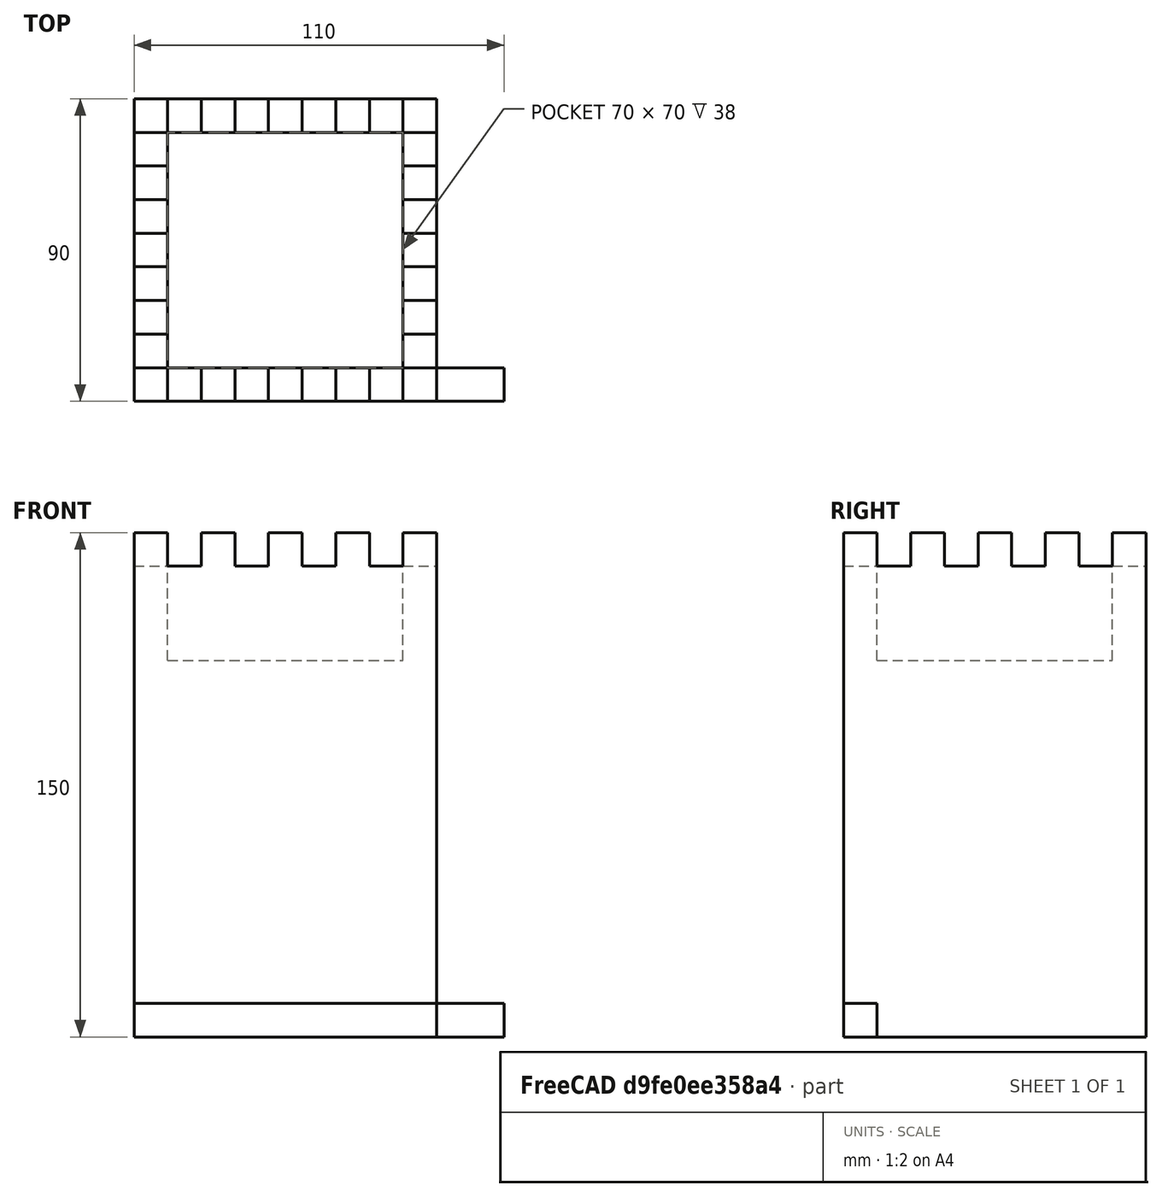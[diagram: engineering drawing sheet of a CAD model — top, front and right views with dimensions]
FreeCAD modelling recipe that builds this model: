
FCSTD DOCUMENT  (FreeCAD 1.0R39285 (Git))
Label: ojt1_t10r02_tower
License: All rights reserved
objects: Part::Box×4, Part::FeaturePython×2, Part::Cut×2, Part::MultiFuse×1
note: 7 computed .brp shape members not serialized (recipe doc carries the construction recipe); baked Part::Feature solids carry a one-line shape summary decoded from their .brp

FEATURE [Part::Box] Box  label="Cub"
  AttacherType = Attacher::AttachEngine3D
  Height = 10
  Length = 110
  Width = 10
FEATURE [Part::FeaturePython] Array  # Draft array (typed FeaturePython)
  AlwaysSyncPlacement = false
  Angle = 360
  ArrayType = 0
  Axis = (0,0,1)
  Base = -> Box
  Center = (0,0,0)
  Count = 4
  ExpandArray = false
  Fuse = false
  IntervalAxis = (0,0,0)
  IntervalX = (0,0,0)
  IntervalY = (0,20,0)
  IntervalZ = (0,0,0)
  NumberCircles = 3
  NumberPolar = 5
  NumberX = 1
  NumberY = 4
  NumberZ = 1
  PlacementList = 4 placements: arithmetic series from (0,0,0) step (0,20,0) to (0,60,0)
  RadialDistance = 50
  ScaleList = (4) [(1,1,1),(1,1,1),(1,1,1),(1,1,1)]
  Symmetry = 1
  TangentialDistance = 25
FEATURE [Part::Box] Box001  label="Cub001"
  AttacherType = Attacher::AttachEngine3D
  Height = 10
  Length = 110
  Width = 10
FEATURE [Part::FeaturePython] Array001  # Draft array (typed FeaturePython)
  AlwaysSyncPlacement = false
  Angle = 360
  ArrayType = 0
  Axis = (0,0,1)
  Base = -> Box001
  Center = (0,0,0)
  Count = 4
  ExpandArray = false
  Fuse = false
  IntervalAxis = (0,0,0)
  IntervalX = (0,0,0)
  IntervalY = (0,20,0)
  IntervalZ = (0,0,0)
  NumberCircles = 3
  NumberPolar = 5
  NumberX = 1
  NumberY = 4
  NumberZ = 1
  Placement = pos=(90,-20,0) rot=(0,0,1;1.5708rad)
  PlacementList = 4 placements: arithmetic series from (0,0,0) step (0,20,0) to (0,60,0)
  RadialDistance = 50
  ScaleList = (4) [(1,1,1),(1,1,1),(1,1,1),(1,1,1)]
  Symmetry = 1
  TangentialDistance = 25
FEATURE [Part::MultiFuse] Fusion
  Placement = pos=(-10,10,140) rot=(0,0,1;0rad)
  Refine = true
  Shapes = -> [Array,Array001]
FEATURE [Part::Box] Box002  label="tower"
  AttacherType = Attacher::AttachEngine3D
  Height = 150
  Length = 90
  Width = 90
FEATURE [Part::Box] Box003  label="Cub002"
  AttacherType = Attacher::AttachEngine3D
  Height = 60
  Length = 70
  Placement = pos=(10,10,112) rot=(0,0,1;0rad)
  Width = 70
FEATURE [Part::Cut] Cut
  Base = -> Box002
  Refine = true
  Tool = -> Box003
FEATURE [Part::Cut] Cut001  label="tower with battelment"
  Base = -> Cut
  Refine = true
  Tool = -> Fusion
